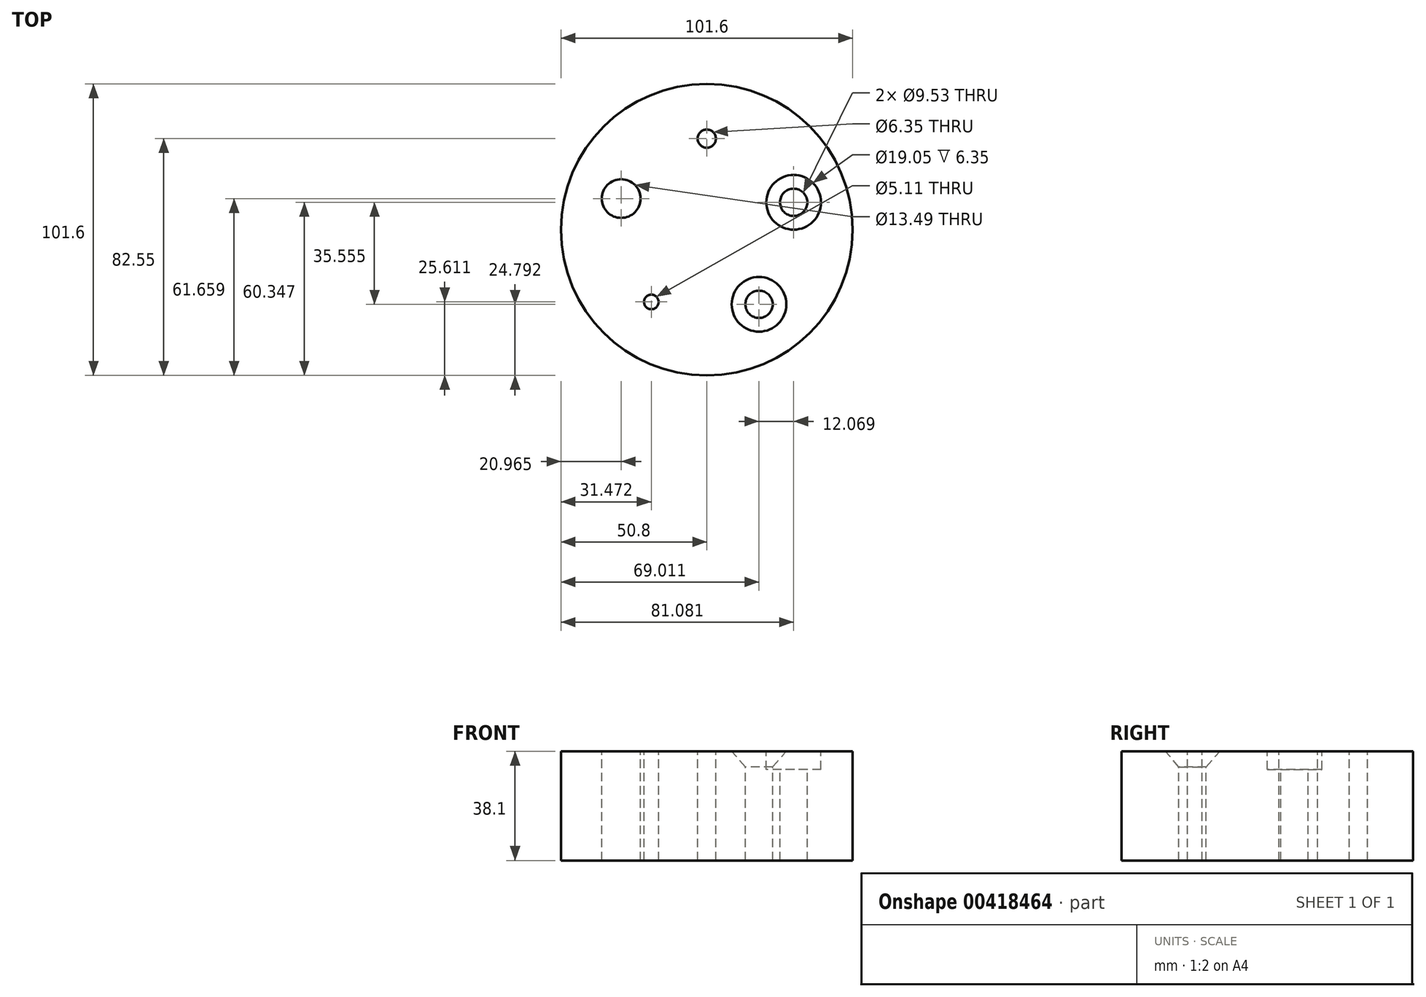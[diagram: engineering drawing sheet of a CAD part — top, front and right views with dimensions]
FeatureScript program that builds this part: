
annotation { "Feature Type Name" : "Feature", "Feature Type Description" : "" }
export const myFeature = defineFeature(function(context is Context, id is Id, definition is map)
    precondition{}
    {
        {
            var Q0;
            Q0=qCreatedBy(makeId("Top.planeOp"),FACE);
            var sketch = newSketch(context, id + "F0", { "sketchPlane" : qUnion([Q0])});
            skCircle(sketch, "E0", {"center": v(0, 0) * mm, "radius": 50.8 * mm});
            skCircle(sketch, "E1", {"center": v(0, 0) * mm, "radius": 31.75 * mm, "construction": true});
            skPoint(sketch, "E2", {"position": v(0, 31.75) * mm});
            skSolve(sketch);
        }
        {
            var Q0;
            Q0 = qSketchRegion(id + "F0", true);
            extrude(context, id + "F1", {"entities" : qUnion([Q0]), "depth" : 38.1 * mm});
        }
        {
            var Q0;
            Q0=qCreatedBy(makeId("Top.planeOp"),FACE);
            cPlane(context, id + "F2", {"entities" : qUnion([Q0]), "cplaneType" : CPlaneType.OFFSET, "offset" : 38.1 * mm, "width" : 152.4 * mm, "height" : 152.4 * mm});
        }
        {
            var Q0;
            Q0=qCreatedBy(id+"F2.planeOp",FACE);
            var sketch = newSketch(context, id + "F3", { "sketchPlane" : qUnion([Q0])});
            skPoint(sketch, "E3", {"position": v(0, 0) * mm});
            skPoint(sketch, "E4", {"position": v(0, 31.75) * mm});
            skPoint(sketch, "E5.1.0", {"position": v(30.28, 9.55) * mm});
            skPoint(sketch, "E5.2.0", {"position": v(18.21, -26) * mm});
            skPoint(sketch, "E5.3.0", {"position": v(-19.33, -25.19) * mm});
            skPoint(sketch, "E5.4.0", {"position": v(-29.84, 10.86) * mm});
            skLineSegment(sketch, "E5.anchor1", {"start": v(0, 0) * mm, "end": v(0, 31.75) * mm, "construction": true});
            skLineSegment(sketch, "E5.anchor2", {"start": v(0, 0) * mm, "end": v(-29.84, 10.86) * mm, "construction": true});
            skSolve(sketch);
        }
        {
            var Q0;
            Q0=sQuery(id+"F3.wireOp",VERTEX,"E4");
            var Q1;
            Q1=makeQuery(id+"F1.opExtrude","SWEPT_BODY",BODY,{"disambiguationData":[OSD([sQuery(id+"F0.wireOp",EDGE,"E0")])]});
            hole(context, id + "F4", {"style" : HoleStyle.SIMPLE, "endStyle" : HoleEndStyle.THROUGH, "holeDiameter" : 6.35 * mm, "isTappedThrough" : true, "tappedDepth" : 12.7 * mm, "tapClearance" : 3, "locations" : qUnion([Q0]), "scope" : qUnion([Q1])});
        }
        {
            var Q0;
            Q0=sQuery(id+"F3.wireOp",VERTEX,"E5.1.0");
            var Q1;
            Q1=makeQuery(id+"F1.opExtrude","SWEPT_BODY",BODY,{"disambiguationData":[OSD([sQuery(id+"F0.wireOp",EDGE,"E0")])]});
            hole(context, id + "F5", {"style" : HoleStyle.C_BORE, "endStyle" : HoleEndStyle.THROUGH, "holeDiameter" : 9.52 * mm, "cBoreDiameter" : 19.05 * mm, "cBoreDepth" : 6.35 * mm, "isTappedThrough" : true, "tappedDepth" : 12.7 * mm, "tapClearance" : 3, "locations" : qUnion([Q0]), "scope" : qUnion([Q1])});
        }
        {
            var Q0;
            Q0=sQuery(id+"F3.wireOp",VERTEX,"E5.2.0");
            var Q1;
            Q1=makeQuery(id+"F1.opExtrude","SWEPT_BODY",BODY,{"disambiguationData":[OSD([sQuery(id+"F0.wireOp",EDGE,"E0")])]});
            hole(context, id + "F6", {"style" : HoleStyle.C_SINK, "endStyle" : HoleEndStyle.THROUGH, "holeDiameter" : 9.52 * mm, "cSinkDiameter" : 19.05 * mm, "cSinkAngle" : 82 * degree, "isTappedThrough" : true, "tappedDepth" : 12.7 * mm, "tapClearance" : 3, "locations" : qUnion([Q0]), "scope" : qUnion([Q1])});
        }
        {
            var Q0;
            Q0=sQuery(id+"F3.wireOp",VERTEX,"E5.3.0");
            var Q1;
            Q1=makeQuery(id+"F1.opExtrude","SWEPT_BODY",BODY,{"disambiguationData":[OSD([sQuery(id+"F0.wireOp",EDGE,"E0")])]});
            hole(context, id + "F7", {"style" : HoleStyle.SIMPLE, "endStyle" : HoleEndStyle.THROUGH, "standardTappedOrClearance" : lookupTablePath({ "standard" : "ANSI", "engagement" : "75%", "pitch" : "20 tpi", "size" : "1/4", "type" : "Tapped" }), "standardBlindInLast" : lookupTablePath({ "standard" : "ANSI", "engagement" : "75%", "pitch" : "20 tpi", "size" : "1/4", "type" : "Tapped" }), "holeDiameter" : 5.1 * mm, "showTappedDepth" : true, "isTappedThrough" : true, "tappedDepth" : 12.7 * mm, "tapClearance" : 3, "locations" : qUnion([Q0]), "scope" : qUnion([Q1]), "majorDiameter" : 6.35 * mm});
        }
        {
            var Q0;
            Q0=sQuery(id+"F3.wireOp",VERTEX,"E5.4.0");
            var Q1;
            Q1=makeQuery(id+"F1.opExtrude","SWEPT_BODY",BODY,{"disambiguationData":[OSD([sQuery(id+"F0.wireOp",EDGE,"E0")])]});
            hole(context, id + "F8", {"style" : HoleStyle.SIMPLE, "endStyle" : HoleEndStyle.THROUGH, "standardTappedOrClearance" : lookupTablePath({ "standard" : "ANSI", "fit" : "Normal (ASME)", "size" : "1/2", "type" : "Clearance" }), "standardBlindInLast" : lookupTablePath({ "fit" : "Free", "standard" : "ANSI", "size" : "1/2", "type" : "Clearance" }), "holeDiameter" : 13.5 * mm, "isTappedThrough" : true, "tappedDepth" : 12.7 * mm, "tapClearance" : 3, "locations" : qUnion([Q0]), "scope" : qUnion([Q1])});
        }
    });
